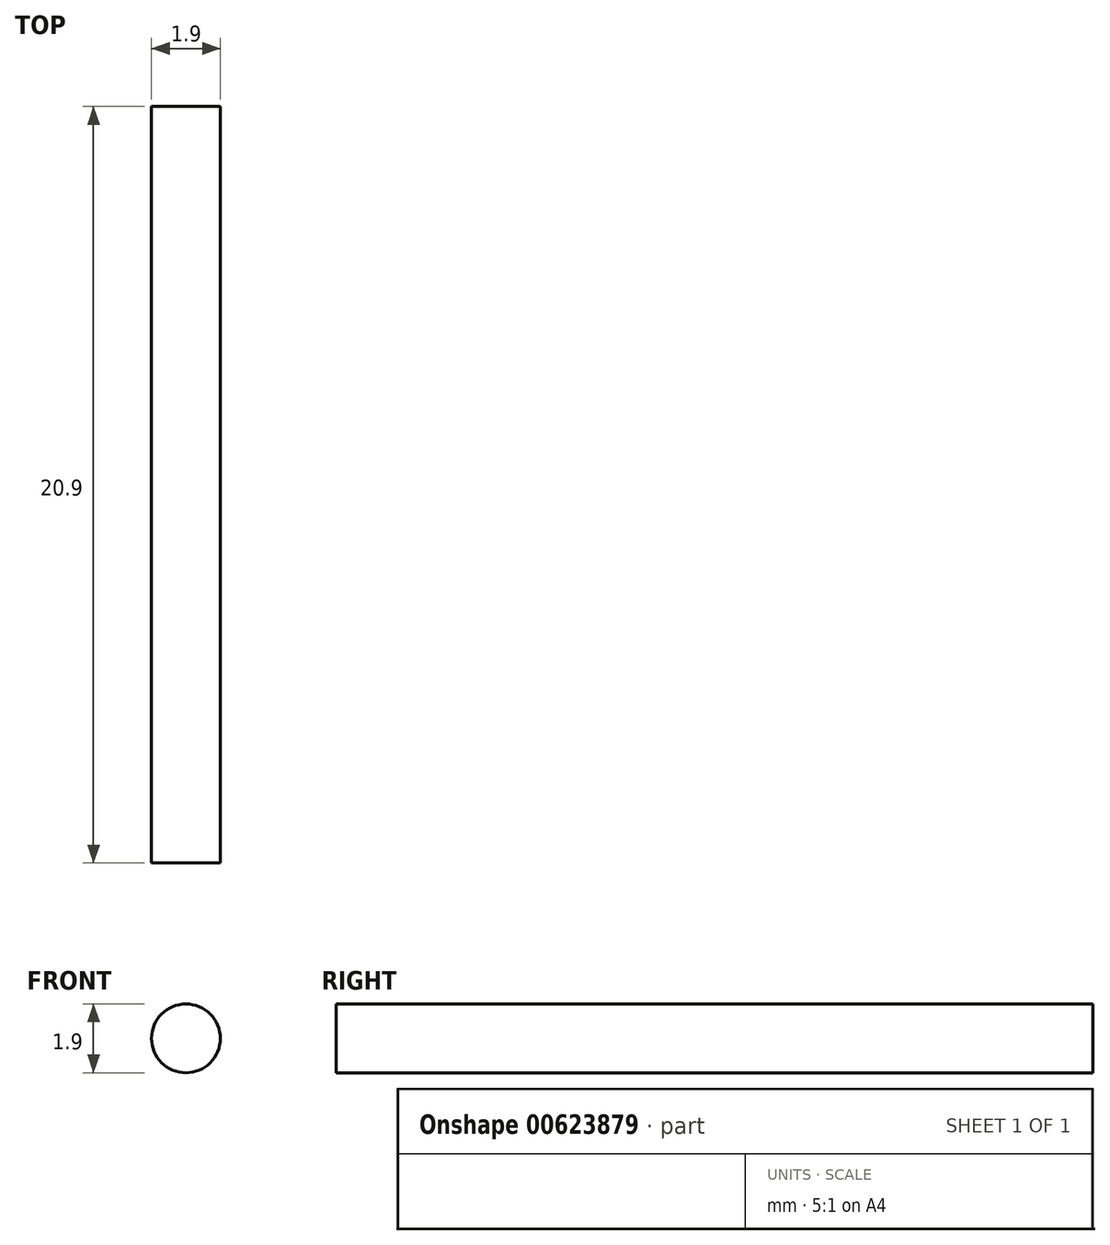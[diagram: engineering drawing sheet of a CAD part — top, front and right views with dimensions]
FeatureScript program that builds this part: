
annotation { "Feature Type Name" : "Feature", "Feature Type Description" : "" }
export const myFeature = defineFeature(function(context is Context, id is Id, definition is map)
    precondition{}
    {
        {
            var Q0;
            Q0=qCreatedBy(makeId("Front.planeOp"),FACE);
            var sketch = newSketch(context, id + "F0", { "sketchPlane" : qUnion([Q0])});
            skCircle(sketch, "E0", {"center": v(0, 0) * mm, "radius": 0.95 * mm});
            skSolve(sketch);
        }
        {
            var Q0;
            Q0 = qSketchRegion(id + "F0", true);
            extrude(context, id + "F1", {"entities" : qUnion([Q0]), "depth" : 20.9 * mm, "offsetDistance" : 25 * mm});
        }
    });
